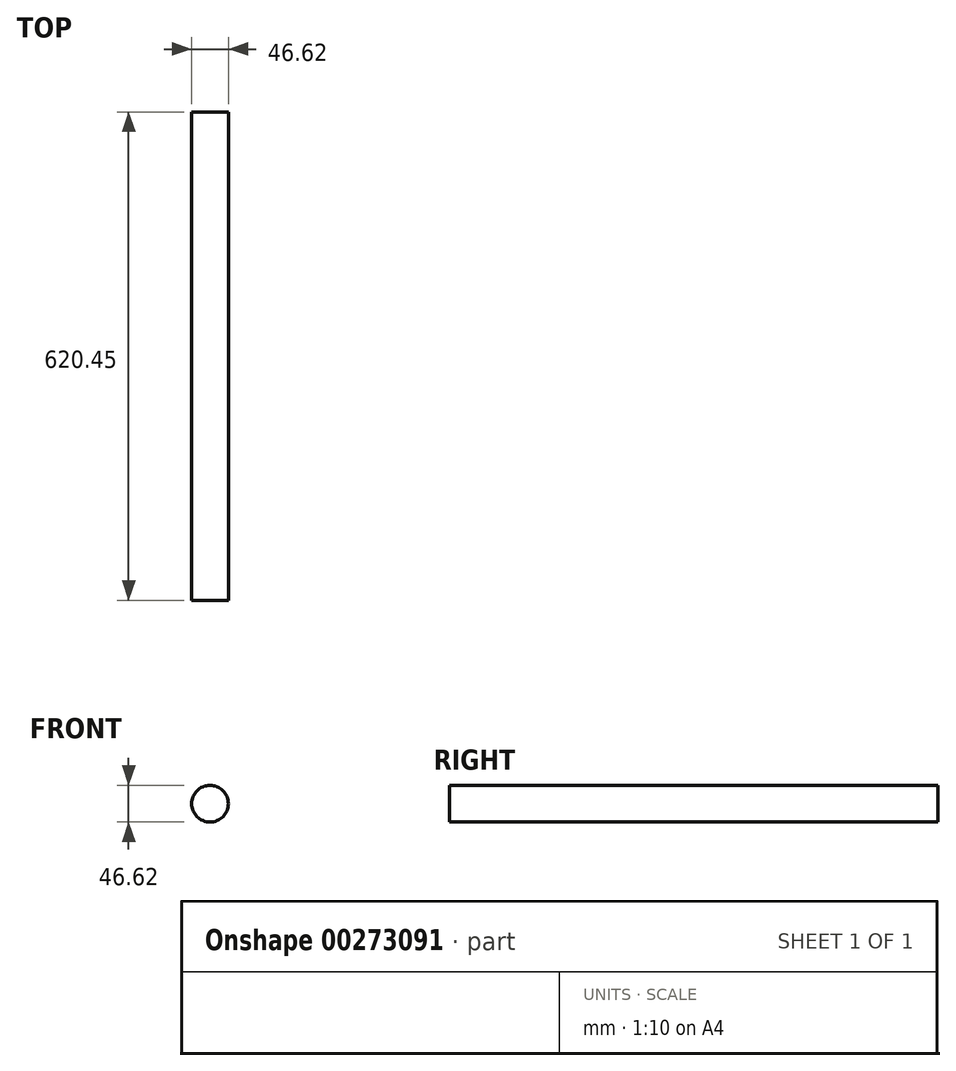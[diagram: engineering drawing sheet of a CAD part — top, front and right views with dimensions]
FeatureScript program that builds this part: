
annotation { "Feature Type Name" : "Feature", "Feature Type Description" : "" }
export const myFeature = defineFeature(function(context is Context, id is Id, definition is map)
    precondition{}
    {
        {
            var Q0;
            Q0=qCreatedBy(makeId("Front.planeOp"),FACE);
            var sketch = newSketch(context, id + "F0", { "sketchPlane" : qUnion([Q0])});
            skCircle(sketch, "E0", {"center": v(0, 0) * mm, "radius": 23.31 * mm});
            skSolve(sketch);
        }
        {
            var Q0;
            Q0 = qSketchRegion(id + "F0", true);
            extrude(context, id + "F1", {"entities" : qUnion([Q0]), "depth" : 620.45 * mm});
        }
    });
